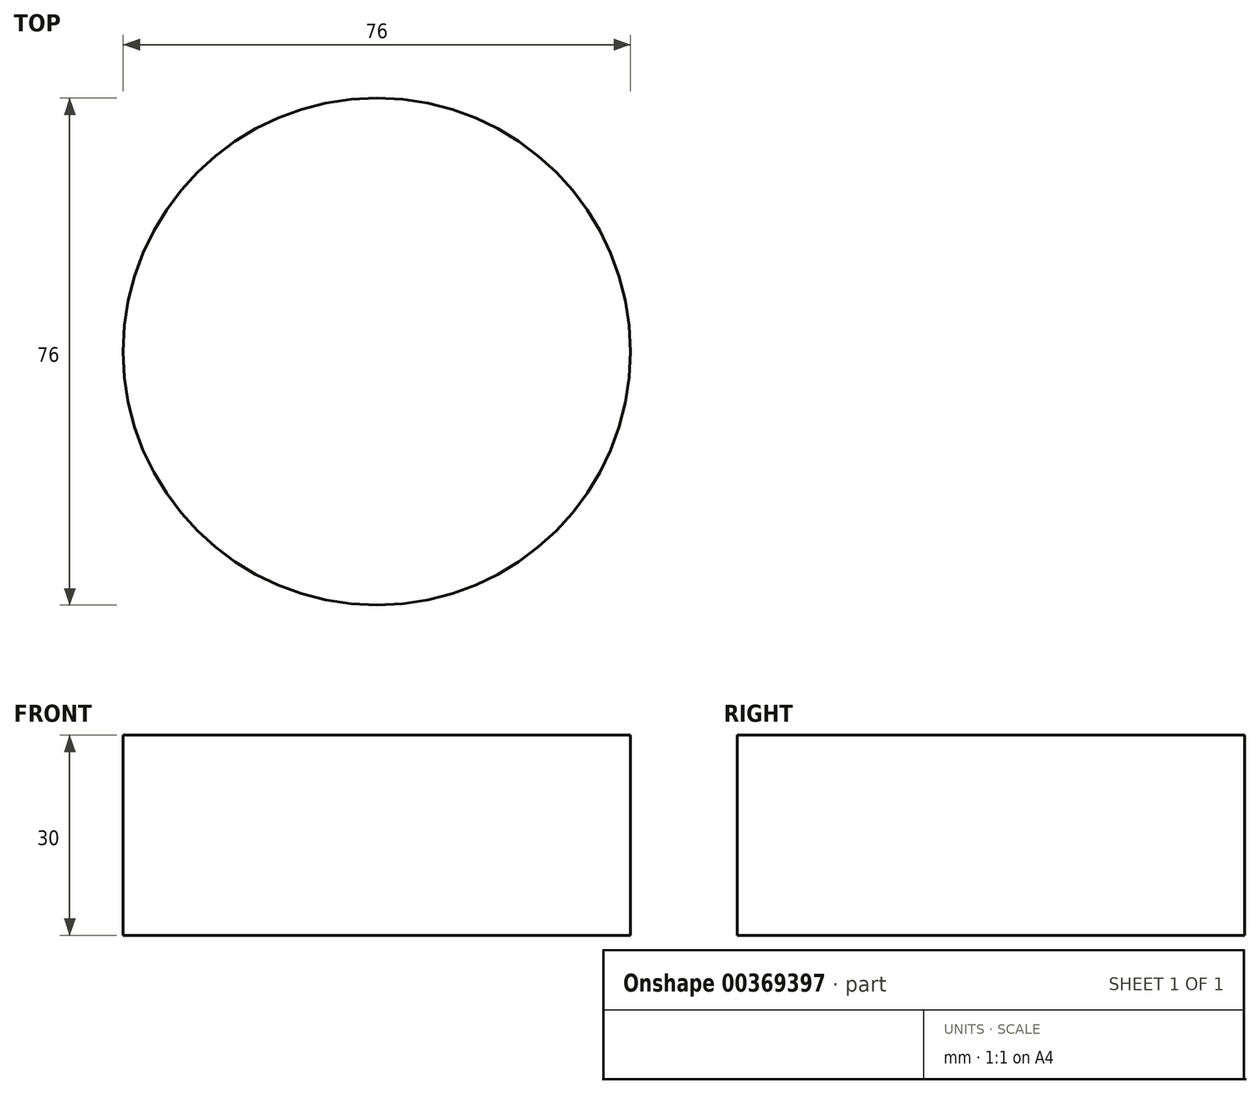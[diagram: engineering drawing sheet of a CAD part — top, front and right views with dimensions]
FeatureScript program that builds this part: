
annotation { "Feature Type Name" : "Feature", "Feature Type Description" : "" }
export const myFeature = defineFeature(function(context is Context, id is Id, definition is map)
    precondition{}
    {
        {
            var Q0;
            Q0=qCreatedBy(makeId("Top.planeOp"),FACE);
            var sketch = newSketch(context, id + "F0", { "sketchPlane" : qUnion([Q0])});
            skCircle(sketch, "E0", {"center": v(0, 0) * mm, "radius": 38 * mm});
            skSolve(sketch);
        }
        {
            var Q0;
            Q0=makeQuery(id+"F0.imprint","IMPRINT",FACE,{"disambiguationData":[TD([[makeQuery(id+"F0.imprint","IMPRINT",EDGE,{"derivedFrom":sQuery(id+"F0.wireOp",EDGE,"E0")}),1.0]])]});
            extrude(context, id + "F1", {"entities" : qUnion([Q0]), "depth" : 30 * mm});
        }
    });
